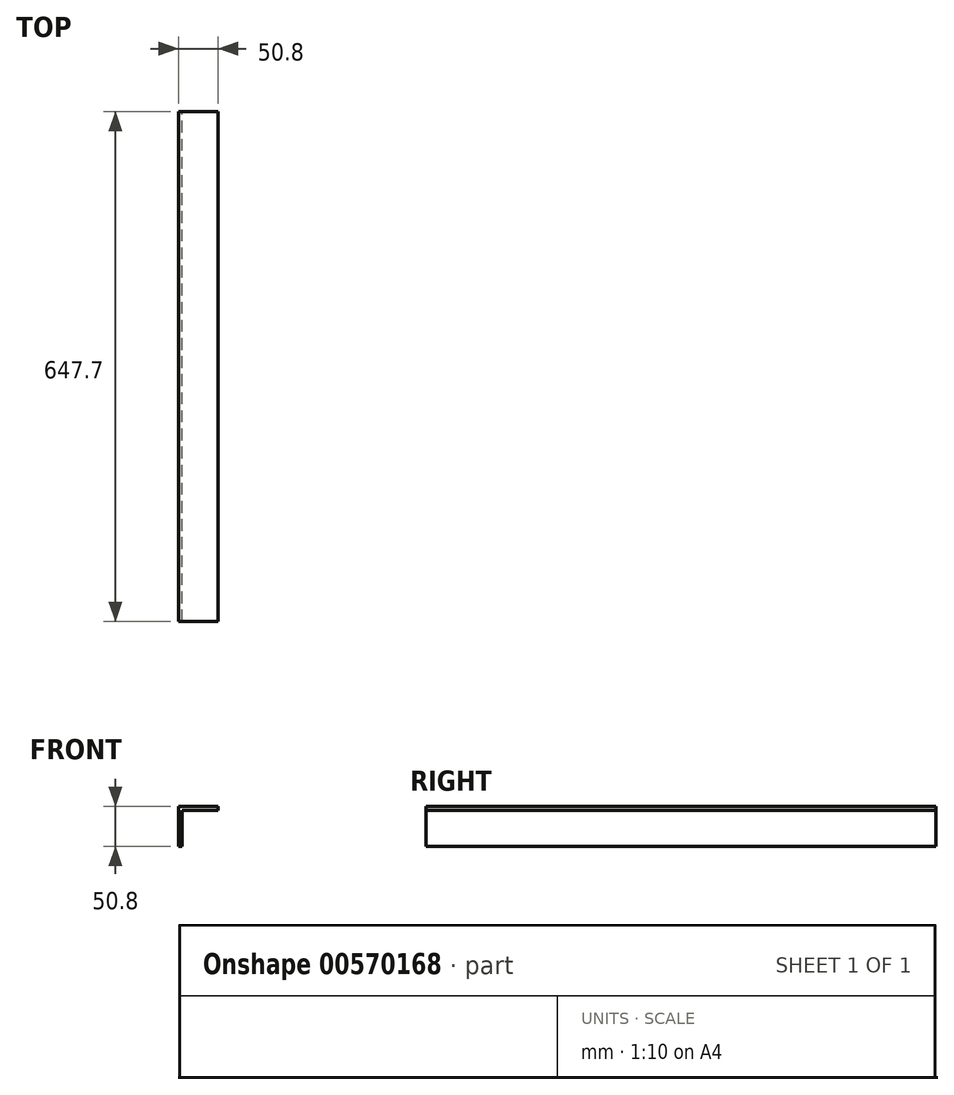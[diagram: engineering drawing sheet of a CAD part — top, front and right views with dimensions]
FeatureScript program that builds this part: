
annotation { "Feature Type Name" : "Feature", "Feature Type Description" : "" }
export const myFeature = defineFeature(function(context is Context, id is Id, definition is map)
    precondition{}
    {
        {
            var Q0;
            Q0=qCreatedBy(makeId("Front.planeOp"),FACE);
            var sketch = newSketch(context, id + "F0", { "sketchPlane" : qUnion([Q0])});
            skLineSegment(sketch, "E0", {"start": v(0, 0) * mm, "end": v(0, 50.8) * mm});
            skLineSegment(sketch, "E1", {"start": v(0, 50.8) * mm, "end": v(50.8, 50.8) * mm});
            skLineSegment(sketch, "E2", {"start": v(50.8, 50.8) * mm, "end": v(50.8, 46.04) * mm});
            skLineSegment(sketch, "E3", {"start": v(50.8, 46.04) * mm, "end": v(4.76, 46.04) * mm});
            skLineSegment(sketch, "E4", {"start": v(4.76, 46.04) * mm, "end": v(4.76, 0) * mm});
            skLineSegment(sketch, "E5", {"start": v(4.76, 0) * mm, "end": v(0, 0) * mm});
            skSolve(sketch);
        }
        {
            var Q0;
            Q0=makeQuery(id+"F0.imprint","IMPRINT",FACE,{"disambiguationData":[TD([[makeQuery(id+"F0.imprint","IMPRINT",EDGE,{"derivedFrom":sQuery(id+"F0.wireOp",EDGE,"E0")}),-1.0]])]});
            extrude(context, id + "F1", {"entities" : qUnion([Q0]), "depth" : 647.7 * mm, "offsetDistance" : 25.4 * mm});
        }
    });
